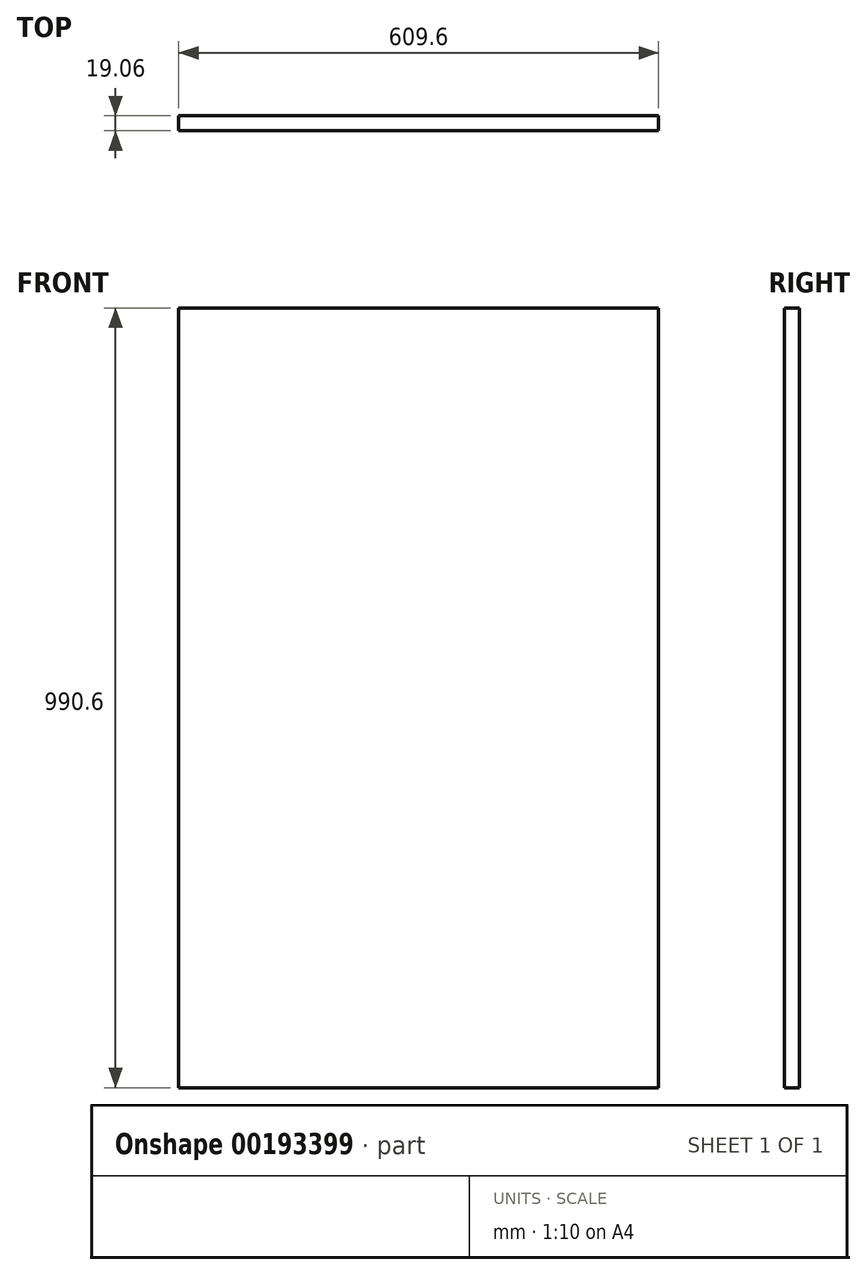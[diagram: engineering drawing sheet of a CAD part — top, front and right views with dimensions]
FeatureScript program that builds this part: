
annotation { "Feature Type Name" : "Feature", "Feature Type Description" : "" }
export const myFeature = defineFeature(function(context is Context, id is Id, definition is map)
    precondition{}
    {
        {
            var Q0;
            Q0=qCreatedBy(makeId("Front.planeOp"),FACE);
            var sketch = newSketch(context, id + "F0", { "sketchPlane" : qUnion([Q0])});
            skLineSegment(sketch, "E0.bottom", {"start": v(-304.8, 495.3) * mm, "end": v(304.8, 495.3) * mm});
            skLineSegment(sketch, "E0.top", {"start": v(-304.8, -495.3) * mm, "end": v(304.8, -495.3) * mm});
            skLineSegment(sketch, "E0.left", {"start": v(-304.8, 495.3) * mm, "end": v(-304.8, -495.3) * mm});
            skLineSegment(sketch, "E0.right", {"start": v(304.8, 495.3) * mm, "end": v(304.8, -495.3) * mm});
            skPoint(sketch, "E0.middle", {"position": v(0, 0) * mm});
            skSolve(sketch);
        }
        {
            var Q0;
            Q0 = qSketchRegion(id + "F0", true);
            extrude(context, id + "F1", {"entities" : qUnion([Q0]), "depth" : 19.05 * mm, "symmetric" : true});
        }
    });
